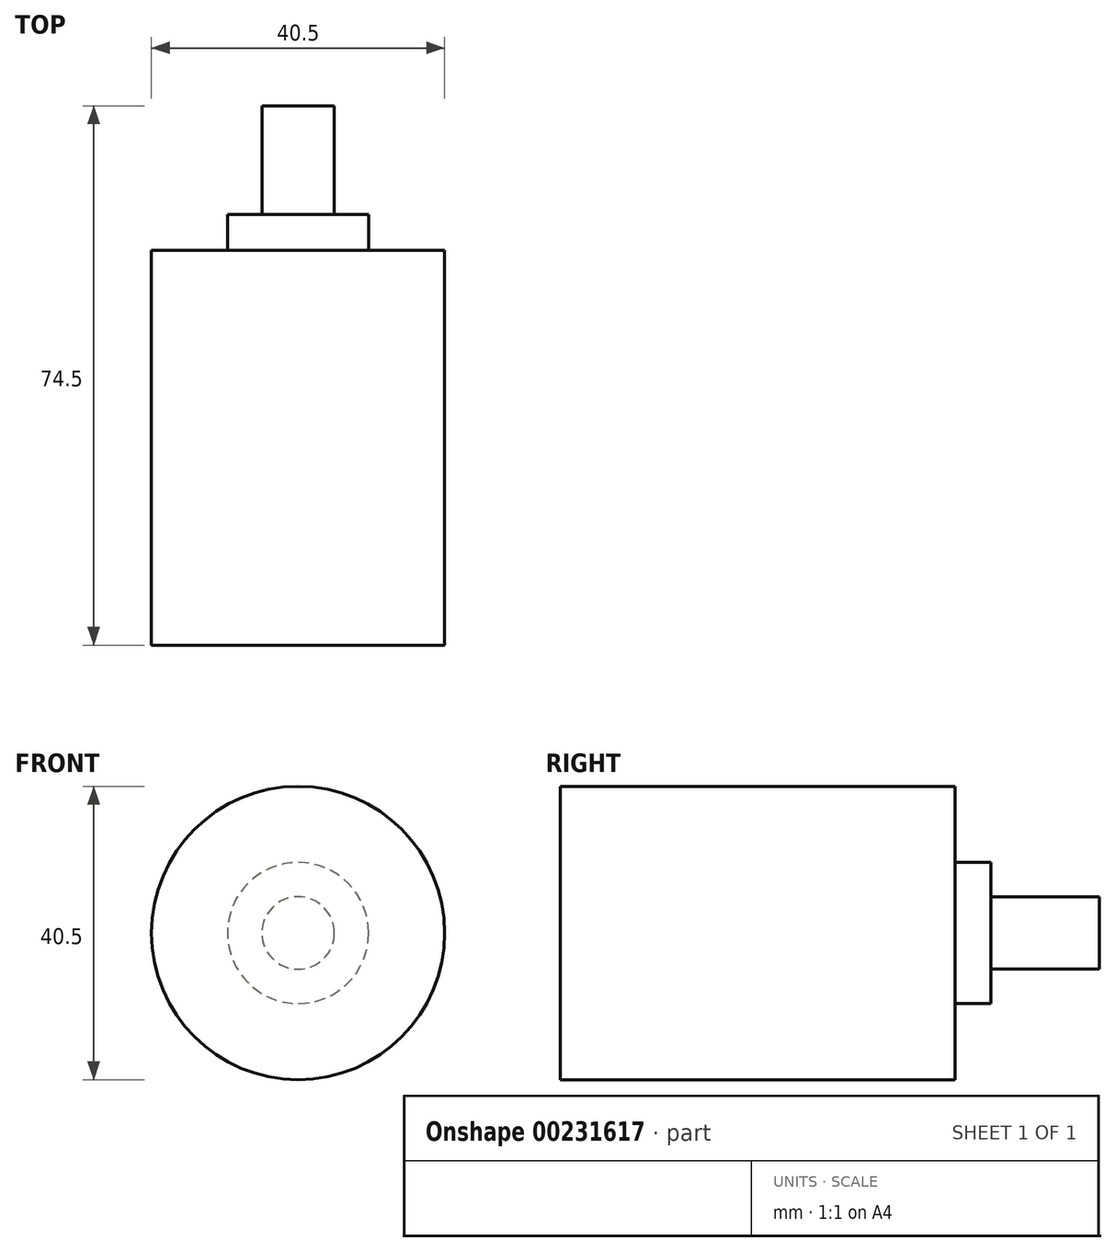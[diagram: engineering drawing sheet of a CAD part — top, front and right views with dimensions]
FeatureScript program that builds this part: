
annotation { "Feature Type Name" : "Feature", "Feature Type Description" : "" }
export const myFeature = defineFeature(function(context is Context, id is Id, definition is map)
    precondition{}
    {
        {
            var Q0;
            Q0=qCreatedBy(makeId("Front.planeOp"),FACE);
            var sketch = newSketch(context, id + "F0", { "sketchPlane" : qUnion([Q0])});
            skCircle(sketch, "E0", {"center": v(0, 0) * mm, "radius": 20.25 * mm});
            skSolve(sketch);
        }
        {
            var Q0;
            Q0 = qSketchRegion(id + "F0", true);
            extrude(context, id + "F1", {"entities" : qUnion([Q0]), "depth" : 54.5 * mm});
        }
        {
            var Q0;
            Q0=makeQuery(id+"F1.opExtrude","CAP_FACE",FACE,{"disambiguationData":[OSD([sQuery(id+"F0.wireOp",EDGE,"E0")])],"isStart":true});
            var sketch = newSketch(context, id + "F2", { "sketchPlane" : qUnion([Q0])});
            skCircle(sketch, "E1", {"center": v(0, 0) * mm, "radius": 9.75 * mm});
            skSolve(sketch);
        }
        {
            var Q0;
            Q0=makeQuery(id+"F2.imprint","IMPRINT",FACE,{"disambiguationData":[TD([[makeQuery(id+"F2.imprint","IMPRINT",EDGE,{"derivedFrom":sQuery(id+"F2.wireOp",EDGE,"E1")}),1.0]])]});
            extrude(context, id + "F3", {"entities" : qUnion([Q0]), "operationType" : NewBodyOperationType.ADD, "depth" : 5 * mm});
        }
        {
            var Q0;
            Q0=makeQuery(id+"F3.opExtrude","CAP_FACE",FACE,{"disambiguationData":[OSD([sQuery(id+"F2.wireOp",EDGE,"E1")])],"isStart":false});
            var sketch = newSketch(context, id + "F4", { "sketchPlane" : qUnion([Q0])});
            skCircle(sketch, "E2", {"center": v(0, 0) * mm, "radius": 5 * mm});
            skSolve(sketch);
        }
        {
            var Q0;
            Q0 = qSketchRegion(id + "F4", true);
            extrude(context, id + "F5", {"entities" : qUnion([Q0]), "operationType" : NewBodyOperationType.ADD, "depth" : 15 * mm});
        }
    });
